# Revit family: QMXS
name_source: partatom
category: Mechanical Equipment
units: mm (PartAtom-declared; Revit-internal decimal feet)

## family parameters
Always vertical = Yes
Cut with Voids When Loaded = No
Part Type = Normal
Room Calculation Point = No
Round Connector Dimension = Use Diameter
Shared = No
Work Plane-Based = No

## types (22) — shared parameters
0 = 0' - 0"
1" = 0' - 1"
1.5 = 0' - 1 1/2"
2" = 0' - 2"
2' = 2' - 0"
3" = 0' - 3"
4" = 0' - 4"
C = 0' - 3"
C/2 = 0' - 1 1/2"
Manufacturer = Loren Cook Company
ONE EIGTH = 0' - 0 1/8"
URL = www.lorencook.com

## per-type parameters (varying)
- 90_QMXS: (A-QMX_LENGTH-7"-1")/2=0' - 8 11/16"; (B/2)-.125"=0' - 9 7/8"; (FAN_RADIUS)*.75=0' - 4 13/16"; A=3' - 9 3/4"; A/2=1' - 10 7/8"; B=1' - 8"; B/2=0' - 10"; D=3' - 1 3/8"; D-(G/2)=1' - 11 3/32"; DC/2=0' - 6 13/32"; DUCT_COLLAR=1' - 0 13/16"; E=1' - 10 1/2"; F=1' - 9 1/4"; FAN_DIA=1' - 0 13/16"; FAN_RAD+1.5"=0' - 7 29/32"; FAN_RADIUS=0' - 6 13/32"; FAN_RADIUS/5=0' - 1 9/32"; G=2' - 4 9/16"; G/2=1' - 2 9/32"; MC_LENGTH=1' - 3 29/32"; Model=QMXS; QMX_LENGTH=1' - 7 7/8"; T_SQ=1' - 3 1/2"; T_SQ/2=0' - 7 3/4"; Type Comments=Mixed-Flow Supply Blower Low Pressure Belt Drive Arrangement 9
- 300_QMXS: (A-QMX_LENGTH-7"-1")/2=0' - 11 17/32"; (B/2)-.125"=2' - 2 7/8"; (FAN_RADIUS)*.75=1' - 3 15/16"; A=7' - 1 9/16"; A/2=3' - 6 25/32"; B=4' - 6"; B/2=2' - 3"; D=6' - 10"; D-(G/2)=3' - 9 3/16"; DC/2=1' - 9 1/4"; DUCT_COLLAR=3' - 6 1/2"; E=3' - 4"; F=3' - 1 5/8"; FAN_DIA=3' - 6 1/2"; FAN_RAD+1.5"=1' - 10 3/4"; FAN_RADIUS=1' - 9 1/4"; FAN_RADIUS/5=0' - 4 1/4"; G=6' - 1 5/8"; G/2=3' - 0 13/16"; MC_LENGTH=3' - 7 3/16"; Model=QMXS; QMX_LENGTH=4' - 6"; T_SQ=4' - 1 1/2"; T_SQ/2=2' - 0 3/4"; Type Comments=Mixed-FlowSupply Blower Low Pressure Belt Drive Arrangement 9
- 120_QMXS: (A-QMX_LENGTH-7"-1")/2=0' - 7 3/32"; (B/2)-.125"=0' - 11 7/8"; (FAN_RADIUS)*.75=0' - 6 13/32"; A=3' - 10 11/16"; A/2=1' - 11 11/32"; B=2' - 0"; B/2=1' - 0"; D=3' - 7 5/8"; D-(G/2)=2' - 3 7/32"; DC/2=0' - 8 17/32"; DUCT_COLLAR=1' - 5 1/16"; E=2' - 1 3/8"; F=2' - 0 3/8"; FAN_DIA=1' - 5 1/16"; FAN_RAD+1.5"=0' - 10 1/32"; FAN_RADIUS=0' - 8 17/32"; FAN_RADIUS/5=0' - 1 23/32"; G=2' - 8 13/16"; G/2=1' - 4 13/32"; MC_LENGTH=1' - 7 3/16"; Model=QMXS; QMX_LENGTH=2' - 0"; T_SQ=1' - 7 1/2"; T_SQ/2=0' - 9 3/4"; Type Comments=Mixed-Flow Supply Blower Low Pressure Belt Drive Arrangement 9
- 135_QMXS: (A-QMX_LENGTH-7"-1")/2=0' - 9 1/8"; (B/2)-.125"=1' - 0 7/8"; (FAN_RADIUS)*.75=0' - 7 7/32"; A=4' - 5 3/4"; A/2=2' - 2 7/8"; B=2' - 2"; B/2=1' - 1"; D=3' - 10 1/2"; D-(G/2)=2' - 0 23/32"; DC/2=0' - 9 5/8"; DUCT_COLLAR=1' - 7 1/4"; E=2' - 3 1/4"; F=2' - 1 3/8"; FAN_DIA=1' - 7 1/4"; FAN_RAD+1.5"=0' - 11 1/8"; FAN_RADIUS=0' - 9 5/8"; FAN_RADIUS/5=0' - 1 15/16"; G=3' - 7 9/16"; G/2=1' - 9 25/32"; MC_LENGTH=1' - 9 19/32"; Model=QMXS; QMX_LENGTH=2' - 3"; T_SQ=1' - 9 1/2"; T_SQ/2=0' - 10 3/4"; Type Comments=Mixed-Flow Supply Blower Low Pressure Belt Drive Arrangement 9
- 150_QMXS: (A-QMX_LENGTH-7"-1")/2=0' - 9 1/8"; (B/2)-.125"=1' - 2 7/8"; (FAN_RADIUS)*.75=0' - 8 1/32"; A=4' - 8 3/4"; A/2=2' - 4 3/8"; B=2' - 6"; B/2=1' - 3"; D=4' - 3"; D-(G/2)=2' - 5 7/32"; DC/2=0' - 10 11/16"; DUCT_COLLAR=1' - 9 3/8"; E=2' - 4"; F=2' - 2 1/8"; FAN_DIA=1' - 9 3/8"; FAN_RAD+1.5"=1' - 0 3/16"; FAN_RADIUS=0' - 10 11/16"; FAN_RADIUS/5=0' - 2 1/8"; G=3' - 7 9/16"; G/2=1' - 9 25/32"; MC_LENGTH=2' - 0"; Model=QMXS; QMX_LENGTH=2' - 6"; T_SQ=2' - 1 1/2"; T_SQ/2=1' - 0 3/4"; Type Comments=Mixed-Flow Supply Blower Low Pressure Belt Drive Arrangement 9
- 165_QMXS: (A-QMX_LENGTH-7"-1")/2=0' - 10 1/2"; (B/2)-.125"=1' - 5 3/8"; (FAN_RADIUS)*.75=0' - 8 13/16"; A=5' - 2 1/2"; A/2=2' - 7 1/4"; B=2' - 11"; B/2=1' - 5 1/2"; D=4' - 7"; D-(G/2)=2' - 7 3/16"; DC/2=0' - 11 3/4"; DUCT_COLLAR=1' - 11 1/2"; E=2' - 5 13/16"; F=2' - 3 1/8"; FAN_DIA=1' - 11 1/2"; FAN_RAD+1.5"=1' - 1 1/4"; FAN_RADIUS=0' - 11 3/4"; FAN_RADIUS/5=0' - 2 11/32"; G=3' - 11 5/8"; G/2=1' - 11 13/16"; MC_LENGTH=2' - 2 13/32"; Model=QMXS; QMX_LENGTH=2' - 9"; T_SQ=2' - 6 1/2"; T_SQ/2=1' - 3 1/4"; Type Comments=Mixed-Flow Supply Blower Low Pressure Belt Drive Arrangement 9
- 180_QMXS: (A-QMX_LENGTH-7"-1")/2=1' - 2 5/32"; (B/2)-.125"=1' - 6 3/8"; (FAN_RADIUS)*.75=0' - 9 5/8"; A=5' - 11 13/16"; A/2=2' - 11 29/32"; B=3' - 1"; B/2=1' - 6 1/2"; D=4' - 9 3/4"; D-(G/2)=2' - 7 7/16"; DC/2=1' - 0 13/16"; DUCT_COLLAR=2' - 1 5/8"; E=2' - 6 3/4"; F=2' - 4 1/8"; FAN_DIA=2' - 1 5/8"; FAN_RAD+1.5"=1' - 2 5/16"; FAN_RADIUS=1' - 0 13/16"; FAN_RADIUS/5=0' - 2 9/16"; G=4' - 4 5/8"; G/2=2' - 2 5/16"; MC_LENGTH=2' - 4"; Model=QMXS; QMX_LENGTH=2' - 11"; T_SQ=2' - 8 1/2"; T_SQ/2=1' - 4 1/4"; Type Comments=Mixed-Flow Supply Blower Low Pressure Belt Drive Arrangement 9
- 202_QMXS: (A-QMX_LENGTH-7"-1")/2=1' - 4 9/32"; (B/2)-.125"=1' - 7 7/8"; (FAN_RADIUS)*.75=0' - 9 5/8"; A=6' - 4 1/16"; A/2=3' - 2 1/32"; B=3' - 4"; B/2=1' - 8"; D=5' - 1 13/16"; D-(G/2)=2' - 6 1/2"; DC/2=1' - 2 3/8"; DUCT_COLLAR=2' - 4 3/4"; E=2' - 8 1/8"; F=2' - 5 1/2"; FAN_DIA=2' - 1 5/8"; FAN_RAD+1.5"=1' - 2 5/16"; FAN_RADIUS=1' - 0 13/16"; FAN_RADIUS/5=0' - 2 9/16"; G=5' - 2 5/8"; G/2=2' - 7 5/16"; MC_LENGTH=2' - 4"; Model=QMXS; QMX_LENGTH=2' - 11"; T_SQ=2' - 11 1/2"; T_SQ/2=1' - 5 3/4"; Type Comments=Mixed-Flow Supply Blower Low Pressure Belt Drive Arrangement 9
- 225_QMXS: (A-QMX_LENGTH-7"-1")/2=1' - 3 1/32"; (B/2)-.125"=1' - 9 3/8"; (FAN_RADIUS)*.75=0' - 11 31/32"; A=6' - 7 9/16"; A/2=3' - 3 25/32"; B=3' - 7"; B/2=1' - 9 1/2"; D=5' - 8 1/8"; D-(G/2)=3' - 0 13/16"; DC/2=1' - 3 31/32"; DUCT_COLLAR=2' - 7 15/16"; E=2' - 11 1/2"; F=2' - 9"; FAN_DIA=2' - 7 15/16"; FAN_RAD+1.5"=1' - 5 15/32"; FAN_RADIUS=1' - 3 31/32"; FAN_RADIUS/5=0' - 3 3/16"; G=5' - 2 5/8"; G/2=2' - 7 5/16"; MC_LENGTH=2' - 8 13/16"; Model=QMXS; QMX_LENGTH=3' - 5"; T_SQ=3' - 2 1/2"; T_SQ/2=1' - 7 1/4"; Type Comments=Mixed-Flow Supply Blower Low Pressure Belt Drive Arrangement 9
- 245_QMXS: (A-QMX_LENGTH-7"-1")/2=0' - 11 7/32"; (B/2)-.125"=1' - 10 7/8"; (FAN_RADIUS)*.75=1' - 1 1/32"; A=6' - 3 7/16"; A/2=3' - 1 23/32"; B=3' - 10"; B/2=1' - 11"; D=5' - 11 13/16"; D-(G/2)=2' - 11"; DC/2=1' - 5 3/8"; DUCT_COLLAR=2' - 10 3/4"; E=3' - 0 5/8"; F=2' - 10 1/8"; FAN_DIA=2' - 10 3/4"; FAN_RAD+1.5"=1' - 6 7/8"; FAN_RADIUS=1' - 5 3/8"; FAN_RADIUS/5=0' - 3 15/32"; G=6' - 1 5/8"; G/2=3' - 0 13/16"; MC_LENGTH=2' - 11 19/32"; Model=QMXS; QMX_LENGTH=3' - 8 1/2"; T_SQ=3' - 5 1/2"; T_SQ/2=1' - 8 3/4"; Type Comments=Mixed-Flow Supply Blower Low Pressure Belt Drive Arrangement 9
- 270_QMXS: (A-QMX_LENGTH-7"-1")/2=0' - 11 11/32"; (B/2)-.125"=2' - 0 7/8"; (FAN_RADIUS)*.75=1' - 2 3/8"; A=6' - 6 3/16"; A/2=3' - 3 3/32"; B=4' - 2"; B/2=2' - 1"; D=6' - 4 5/16"; D-(G/2)=3' - 3 1/2"; DC/2=1' - 7 5/32"; DUCT_COLLAR=3' - 2 5/16"; E=3' - 2"; F=2' - 11 9/16"; FAN_DIA=3' - 2 5/16"; FAN_RAD+1.5"=1' - 8 21/32"; FAN_RADIUS=1' - 7 5/32"; FAN_RADIUS/5=0' - 3 27/32"; G=6' - 1 5/8"; G/2=3' - 0 13/16"; MC_LENGTH=3' - 1 19/32"; Model=QMXS; QMX_LENGTH=3' - 11"; T_SQ=3' - 9 1/2"; T_SQ/2=1' - 10 3/4"; Type Comments=Mixed-Flow Supply Blower Low Pressure Belt Drive Arrangement 9
- 120_QMXS-HP: (A-QMX_LENGTH-7"-1")/2=0' - 7 3/32"; (B/2)-.125"=0' - 11 7/8"; (FAN_RADIUS)*.75=0' - 6 13/32"; A=3' - 10 11/16"; A/2=1' - 11 11/32"; B=2' - 0"; B/2=1' - 0"; D=3' - 7 5/8"; D-(G/2)=2' - 3 7/32"; DC/2=0' - 8 17/32"; DUCT_COLLAR=1' - 5 1/16"; E=2' - 1 3/8"; F=2' - 0 3/8"; FAN_DIA=1' - 5 1/16"; FAN_RAD+1.5"=0' - 10 1/32"; FAN_RADIUS=0' - 8 17/32"; FAN_RADIUS/5=0' - 1 23/32"; G=2' - 8 13/16"; G/2=1' - 4 13/32"; MC_LENGTH=1' - 7 3/16"; Model=QMXS-HP; QMX_LENGTH=2' - 0"; T_SQ=1' - 7 1/2"; T_SQ/2=0' - 9 3/4"; Type Comments=Mixed-Flow Supply Blower High Pressure Belt Drive Arrangement 9
- 135_QMXS-HP: (A-QMX_LENGTH-7"-1")/2=0' - 9 1/8"; (B/2)-.125"=1' - 0 7/8"; (FAN_RADIUS)*.75=0' - 7 7/32"; A=4' - 5 3/4"; A/2=2' - 2 7/8"; B=2' - 2"; B/2=1' - 1"; D=3' - 10 1/2"; D-(G/2)=2' - 0 23/32"; DC/2=0' - 9 5/8"; DUCT_COLLAR=1' - 7 1/4"; E=2' - 3 1/4"; F=2' - 1 3/8"; FAN_DIA=1' - 7 1/4"; FAN_RAD+1.5"=0' - 11 1/8"; FAN_RADIUS=0' - 9 5/8"; FAN_RADIUS/5=0' - 1 15/16"; G=3' - 7 9/16"; G/2=1' - 9 25/32"; MC_LENGTH=1' - 9 19/32"; Model=QMXS-HP; QMX_LENGTH=2' - 3"; T_SQ=1' - 9 1/2"; T_SQ/2=0' - 10 3/4"; Type Comments=Mixed-Flow Supply Blower High Pressure Belt Drive Arrangement 9
- 150_QMXS-HP: (A-QMX_LENGTH-7"-1")/2=0' - 9 1/8"; (B/2)-.125"=1' - 2 7/8"; (FAN_RADIUS)*.75=0' - 8 1/32"; A=4' - 8 3/4"; A/2=2' - 4 3/8"; B=2' - 6"; B/2=1' - 3"; D=4' - 3"; D-(G/2)=2' - 5 7/32"; DC/2=0' - 10 11/16"; DUCT_COLLAR=1' - 9 3/8"; E=2' - 4"; F=2' - 2 1/8"; FAN_DIA=1' - 9 3/8"; FAN_RAD+1.5"=1' - 0 3/16"; FAN_RADIUS=0' - 10 11/16"; FAN_RADIUS/5=0' - 2 1/8"; G=3' - 7 9/16"; G/2=1' - 9 25/32"; MC_LENGTH=2' - 0"; Model=QMXS-HP; QMX_LENGTH=2' - 6"; T_SQ=2' - 1 1/2"; T_SQ/2=1' - 0 3/4"; Type Comments=Mixed-Flow Supply Blower High Pressure Belt Drive Arrangement 9
- 165_QMXS-HP: (A-QMX_LENGTH-7"-1")/2=0' - 10 1/2"; (B/2)-.125"=1' - 5 3/8"; (FAN_RADIUS)*.75=0' - 8 13/16"; A=5' - 2 1/2"; A/2=2' - 7 1/4"; B=2' - 11"; B/2=1' - 5 1/2"; D=4' - 7"; D-(G/2)=2' - 7 3/16"; DC/2=0' - 11 3/4"; DUCT_COLLAR=1' - 11 1/2"; E=2' - 5 13/16"; F=2' - 3 1/8"; FAN_DIA=1' - 11 1/2"; FAN_RAD+1.5"=1' - 1 1/4"; FAN_RADIUS=0' - 11 3/4"; FAN_RADIUS/5=0' - 2 11/32"; G=3' - 11 5/8"; G/2=1' - 11 13/16"; MC_LENGTH=2' - 2 13/32"; Model=QMXS-HP; QMX_LENGTH=2' - 9"; T_SQ=2' - 6 1/2"; T_SQ/2=1' - 3 1/4"; Type Comments=Mixed-Flow Supply Blower High Pressure Belt Drive Arrangement 9
- 180_QMXS-HP: (A-QMX_LENGTH-7"-1")/2=1' - 2 5/32"; (B/2)-.125"=1' - 6 3/8"; (FAN_RADIUS)*.75=0' - 9 5/8"; A=5' - 11 13/16"; A/2=2' - 11 29/32"; B=3' - 1"; B/2=1' - 6 1/2"; D=4' - 9 3/4"; D-(G/2)=2' - 7 7/16"; DC/2=1' - 0 13/16"; DUCT_COLLAR=2' - 1 5/8"; E=2' - 6 3/4"; F=2' - 4 1/8"; FAN_DIA=2' - 1 5/8"; FAN_RAD+1.5"=1' - 2 5/16"; FAN_RADIUS=1' - 0 13/16"; FAN_RADIUS/5=0' - 2 9/16"; G=4' - 4 5/8"; G/2=2' - 2 5/16"; MC_LENGTH=2' - 4"; Model=QMXS-HP; QMX_LENGTH=2' - 11"; T_SQ=2' - 8 1/2"; T_SQ/2=1' - 4 1/4"; Type Comments=Mixed-Flow Supply Blower High Pressure Belt Drive Arrangement 9
- 202_QMXS-HP: (A-QMX_LENGTH-7"-1")/2=1' - 4 9/32"; (B/2)-.125"=1' - 7 7/8"; (FAN_RADIUS)*.75=0' - 9 5/8"; A=6' - 4 1/16"; A/2=3' - 2 1/32"; B=3' - 4"; B/2=1' - 8"; D=5' - 1 13/16"; D-(G/2)=2' - 6 1/2"; DC/2=1' - 2 3/8"; DUCT_COLLAR=2' - 4 3/4"; E=2' - 8 1/8"; F=2' - 5 1/2"; FAN_DIA=2' - 1 5/8"; FAN_RAD+1.5"=1' - 2 5/16"; FAN_RADIUS=1' - 0 13/16"; FAN_RADIUS/5=0' - 2 9/16"; G=5' - 2 5/8"; G/2=2' - 7 5/16"; MC_LENGTH=2' - 4"; Model=QMXS-HP; QMX_LENGTH=2' - 11"; T_SQ=2' - 11 1/2"; T_SQ/2=1' - 5 3/4"; Type Comments=Mixed-Flow Supply Blower High Pressure Belt Drive Arrangement 9
- 225_QMXS-HP: (A-QMX_LENGTH-7"-1")/2=1' - 3 1/32"; (B/2)-.125"=1' - 9 3/8"; (FAN_RADIUS)*.75=0' - 11 31/32"; A=6' - 7 9/16"; A/2=3' - 3 25/32"; B=3' - 7"; B/2=1' - 9 1/2"; D=5' - 8 1/8"; D-(G/2)=3' - 0 13/16"; DC/2=1' - 3 31/32"; DUCT_COLLAR=2' - 7 15/16"; E=2' - 11 1/2"; F=2' - 9"; FAN_DIA=2' - 7 15/16"; FAN_RAD+1.5"=1' - 5 15/32"; FAN_RADIUS=1' - 3 31/32"; FAN_RADIUS/5=0' - 3 3/16"; G=5' - 2 5/8"; G/2=2' - 7 5/16"; MC_LENGTH=2' - 8 13/16"; Model=QMXS-HP; QMX_LENGTH=3' - 5"; T_SQ=3' - 2 1/2"; T_SQ/2=1' - 7 1/4"; Type Comments=Mixed-Flow Supply Blower High Pressure Belt Drive Arrangement 9
- 245_QMXS-HP: (A-QMX_LENGTH-7"-1")/2=0' - 11 7/32"; (B/2)-.125"=1' - 10 7/8"; (FAN_RADIUS)*.75=1' - 1 1/32"; A=6' - 3 7/16"; A/2=3' - 1 23/32"; B=3' - 10"; B/2=1' - 11"; D=5' - 11 13/16"; D-(G/2)=2' - 11"; DC/2=1' - 5 3/8"; DUCT_COLLAR=2' - 10 3/4"; E=3' - 0 5/8"; F=2' - 10 1/8"; FAN_DIA=2' - 10 3/4"; FAN_RAD+1.5"=1' - 6 7/8"; FAN_RADIUS=1' - 5 3/8"; FAN_RADIUS/5=0' - 3 15/32"; G=6' - 1 5/8"; G/2=3' - 0 13/16"; MC_LENGTH=2' - 11 19/32"; Model=QMXS-HP; QMX_LENGTH=3' - 8 1/2"; T_SQ=3' - 5 1/2"; T_SQ/2=1' - 8 3/4"; Type Comments=Mixed-Flow Supply Blower High Pressure Belt Drive Arrangement 9
- 270_QMXS-HP: (A-QMX_LENGTH-7"-1")/2=0' - 11 11/32"; (B/2)-.125"=2' - 0 7/8"; (FAN_RADIUS)*.75=1' - 2 3/8"; A=6' - 6 3/16"; A/2=3' - 3 3/32"; B=4' - 2"; B/2=2' - 1"; D=6' - 4 5/16"; D-(G/2)=3' - 3 1/2"; DC/2=1' - 7 5/32"; DUCT_COLLAR=3' - 2 5/16"; E=3' - 2"; F=2' - 11 9/16"; FAN_DIA=3' - 2 5/16"; FAN_RAD+1.5"=1' - 8 21/32"; FAN_RADIUS=1' - 7 5/32"; FAN_RADIUS/5=0' - 3 27/32"; G=6' - 1 5/8"; G/2=3' - 0 13/16"; MC_LENGTH=3' - 1 19/32"; Model=QMXS-HP; QMX_LENGTH=3' - 11"; T_SQ=3' - 9 1/2"; T_SQ/2=1' - 10 3/4"; Type Comments=Mixed-Flow Supply Blower High Pressure Belt Drive Arrangement 9
- 300_QMXS-HP: (A-QMX_LENGTH-7"-1")/2=0' - 11 17/32"; (B/2)-.125"=2' - 2 7/8"; (FAN_RADIUS)*.75=1' - 3 15/16"; A=7' - 1 9/16"; A/2=3' - 6 25/32"; B=4' - 6"; B/2=2' - 3"; D=6' - 10"; D-(G/2)=3' - 9 3/16"; DC/2=1' - 9 1/4"; DUCT_COLLAR=3' - 6 1/2"; E=3' - 4"; F=3' - 1 5/8"; FAN_DIA=3' - 6 1/2"; FAN_RAD+1.5"=1' - 10 3/4"; FAN_RADIUS=1' - 9 1/4"; FAN_RADIUS/5=0' - 4 1/4"; G=6' - 1 5/8"; G/2=3' - 0 13/16"; MC_LENGTH=3' - 7 3/16"; Model=QMXS-HP; QMX_LENGTH=4' - 6"; T_SQ=4' - 1 1/2"; T_SQ/2=2' - 0 3/4"; Type Comments=Mixed-Flow Supply Blower High Pressure Belt Drive Arrangement 9
- 90_QMXS-HP: (A-QMX_LENGTH-7"-1")/2=0' - 8 11/16"; (B/2)-.125"=0' - 9 7/8"; (FAN_RADIUS)*.75=0' - 4 13/16"; A=3' - 9 3/4"; A/2=1' - 10 7/8"; B=1' - 8"; B/2=0' - 10"; D=3' - 1 3/8"; D-(G/2)=1' - 11 3/32"; DC/2=0' - 6 13/32"; DUCT_COLLAR=1' - 0 13/16"; E=1' - 10 1/2"; F=1' - 9 1/4"; FAN_DIA=1' - 0 13/16"; FAN_RAD+1.5"=0' - 7 29/32"; FAN_RADIUS=0' - 6 13/32"; FAN_RADIUS/5=0' - 1 9/32"; G=2' - 4 9/16"; G/2=1' - 2 9/32"; MC_LENGTH=1' - 3 29/32"; Model=QMXS-HP; QMX_LENGTH=1' - 7 7/8"; T_SQ=1' - 3 1/2"; T_SQ/2=0' - 7 3/4"; Type Comments=Mixed-Flow Supply Blower High Pressure Belt Drive Arrangement 9

## geometry (parser evidence)
native form markers: Sweep x1
no freeform markers — native parametric forms only
